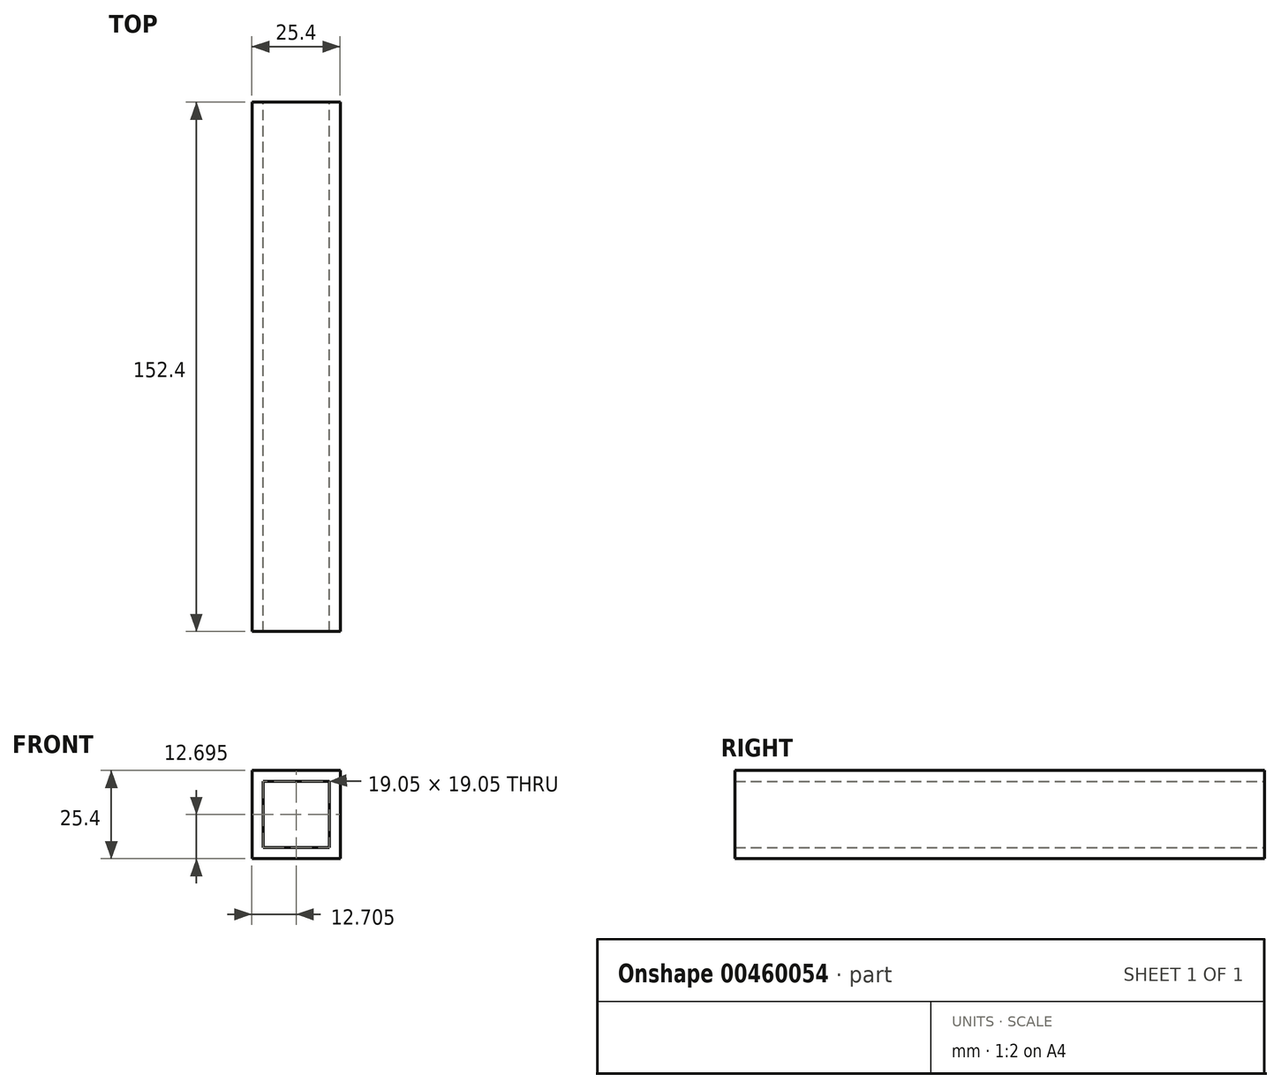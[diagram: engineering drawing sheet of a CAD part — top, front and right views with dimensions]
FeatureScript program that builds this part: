
annotation { "Feature Type Name" : "Feature", "Feature Type Description" : "" }
export const myFeature = defineFeature(function(context is Context, id is Id, definition is map)
    precondition{}
    {
        {
            var Q0;
            Q0=qCreatedBy(makeId("Front.planeOp"),FACE);
            var sketch = newSketch(context, id + "F0", { "sketchPlane" : qUnion([Q0])});
            skLineSegment(sketch, "E0.bottom", {"start": v(-22.23, 22.23) * mm, "end": v(3.17, 22.23) * mm});
            skLineSegment(sketch, "E0.top", {"start": v(-22.23, -3.18) * mm, "end": v(3.18, -3.18) * mm});
            skLineSegment(sketch, "E0.left", {"start": v(-22.23, 22.23) * mm, "end": v(-22.23, -3.18) * mm});
            skLineSegment(sketch, "E0.right", {"start": v(3.17, 22.23) * mm, "end": v(3.18, -3.18) * mm});
            skLineSegment(sketch, "E1.bottom", {"start": v(-19.05, 19.05) * mm, "end": v(0, 19.05) * mm});
            skLineSegment(sketch, "E1.top", {"start": v(-19.05, 0) * mm, "end": v(0, 0) * mm});
            skLineSegment(sketch, "E1.left", {"start": v(-19.05, 19.05) * mm, "end": v(-19.05, 0) * mm});
            skLineSegment(sketch, "E1.right", {"start": v(0, 19.05) * mm, "end": v(0, 0) * mm});
            skSolve(sketch);
        }
        {
            var Q0;
            Q0=qSketchRegion(id+"F0",true);
            extrude(context, id + "F1", {"entities" : qUnion([Q0]), "depth" : 152.4 * mm});
        }
    });
